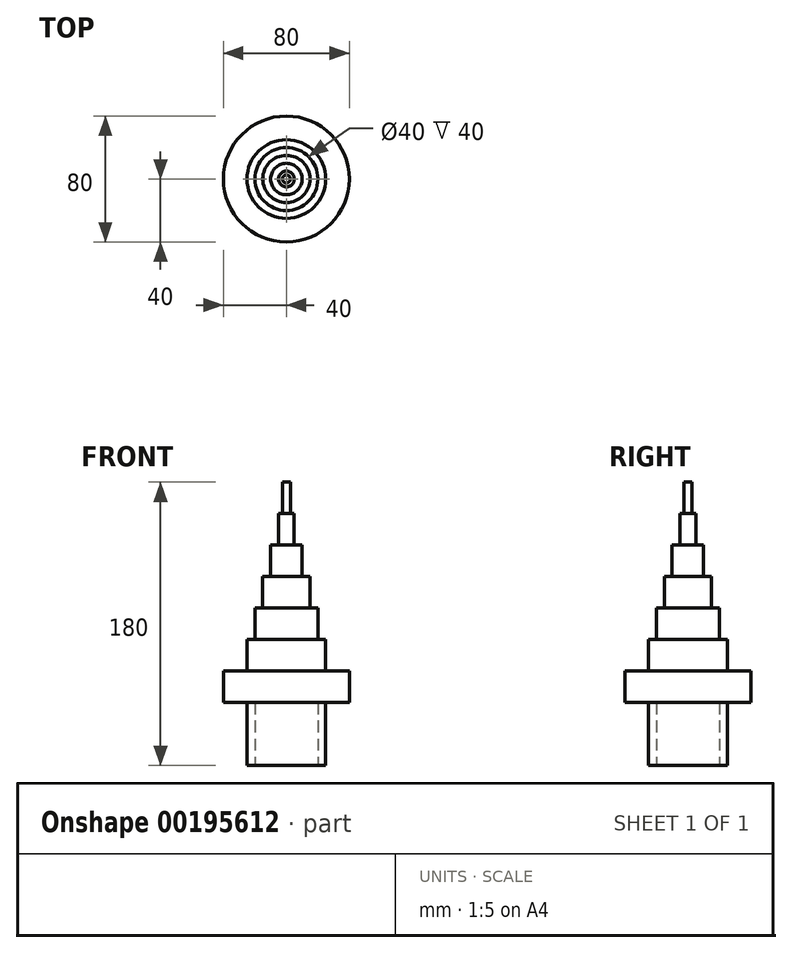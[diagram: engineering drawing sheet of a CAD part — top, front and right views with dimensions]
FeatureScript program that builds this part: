
annotation { "Feature Type Name" : "Feature", "Feature Type Description" : "" }
export const myFeature = defineFeature(function(context is Context, id is Id, definition is map)
    precondition{}
    {
        {
            var Q0;
            Q0=qCreatedBy(makeId("Front.planeOp"),FACE);
            var sketch = newSketch(context, id + "F0", { "sketchPlane" : qUnion([Q0])});
            skLineSegment(sketch, "E0", {"start": v(0, 0) * mm, "end": v(-25, 0) * mm});
            skLineSegment(sketch, "E1", {"start": v(-25, 0) * mm, "end": v(-25, 40) * mm});
            skLineSegment(sketch, "E2", {"start": v(-25, 40) * mm, "end": v(-40, 40) * mm});
            skLineSegment(sketch, "E3", {"start": v(-40, 40) * mm, "end": v(-40, 60) * mm});
            skLineSegment(sketch, "E4", {"start": v(-25, 60) * mm, "end": v(-40, 60) * mm});
            skLineSegment(sketch, "E5", {"start": v(-25, 60) * mm, "end": v(-25, 80) * mm});
            skLineSegment(sketch, "E6", {"start": v(-25, 80) * mm, "end": v(-20, 80) * mm});
            skLineSegment(sketch, "E7", {"start": v(-20, 80) * mm, "end": v(-20, 100) * mm});
            skLineSegment(sketch, "E8", {"start": v(-10, 120) * mm, "end": v(-10, 140) * mm});
            skLineSegment(sketch, "E9", {"start": v(-10, 140) * mm, "end": v(-5, 140) * mm});
            skLineSegment(sketch, "E10", {"start": v(-5, 140) * mm, "end": v(-5, 160) * mm});
            skLineSegment(sketch, "E11", {"start": v(-5, 160) * mm, "end": v(-2.5, 160) * mm});
            skLineSegment(sketch, "E12", {"start": v(-2.5, 160) * mm, "end": v(-2.5, 180) * mm});
            skLineSegment(sketch, "E13", {"start": v(-2.5, 180) * mm, "end": v(0, 180) * mm});
            skLineSegment(sketch, "E14", {"start": v(0, 0) * mm, "end": v(0, 180) * mm});
            skLineSegment(sketch, "E15", {"start": v(-20, 100) * mm, "end": v(-15, 100) * mm});
            skLineSegment(sketch, "E16", {"start": v(-15, 100) * mm, "end": v(-15, 120) * mm});
            skLineSegment(sketch, "E17", {"start": v(-15, 120) * mm, "end": v(-10, 120) * mm});
            skSolve(sketch);
        }
        {
            var Q0;
            Q0 = qSketchRegion(id + "F0", true);
            var Q1;
            Q1=sQuery(id+"F0.wireOp",EDGE,"E14");
            revolve(context, id + "F1", {"entities" : qUnion([Q0]), "axis" : qUnion([Q1]), "revolveType" : RevolveType.FULL});
        }
        {
            var Q0;
            Q0=makeQuery(id+"F1.opRevolve","SWEPT_FACE",FACE,{"disambiguationData":[OSD([sQuery(id+"F0.wireOp",EDGE,"E0")])]});
            var sketch = newSketch(context, id + "F2", { "sketchPlane" : qUnion([Q0])});
            skCircle(sketch, "E18", {"center": v(0, 0) * mm, "radius": 20 * mm});
            skSolve(sketch);
        }
        {
            var Q0;
            Q0 = qSketchRegion(id + "F2", true);
            extrude(context, id + "F3", {"entities" : qUnion([Q0]), "operationType" : NewBodyOperationType.REMOVE, "oppositeDirection" : true, "depth" : 40 * mm});
        }
    });
